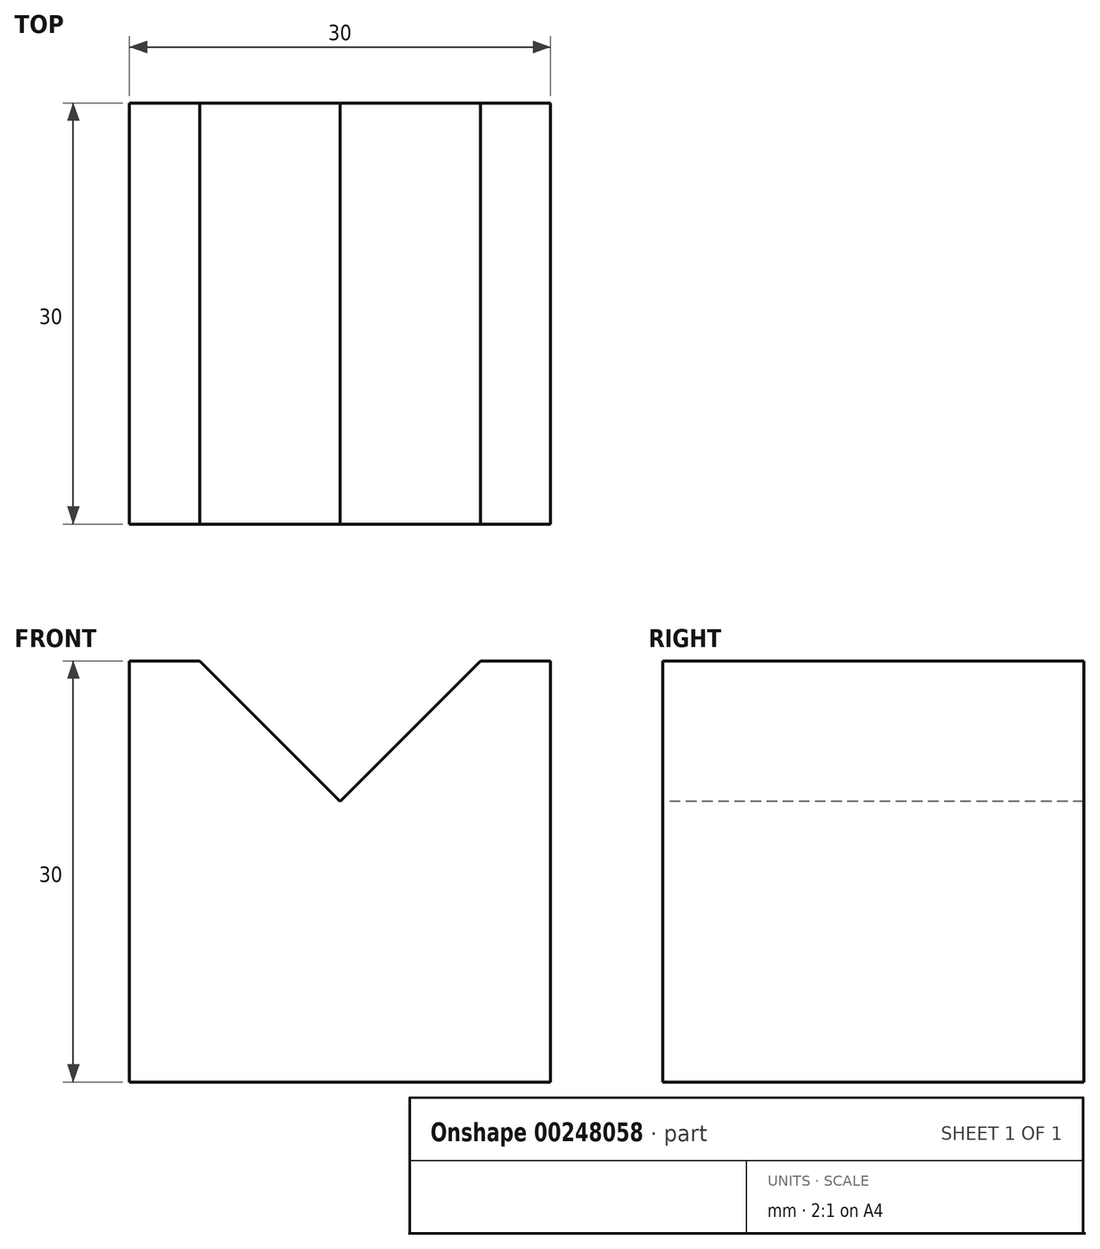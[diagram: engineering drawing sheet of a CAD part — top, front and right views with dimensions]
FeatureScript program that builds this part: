
annotation { "Feature Type Name" : "Feature", "Feature Type Description" : "" }
export const myFeature = defineFeature(function(context is Context, id is Id, definition is map)
    precondition{}
    {
        {
            var Q0;
            Q0=qCreatedBy(makeId("Top.planeOp"),FACE);
            var sketch = newSketch(context, id + "F0", { "sketchPlane" : qUnion([Q0])});
            skLineSegment(sketch, "E0.bottom", {"start": v(15, 15) * mm, "end": v(-15, 15) * mm});
            skLineSegment(sketch, "E0.top", {"start": v(15, -15) * mm, "end": v(-15, -15) * mm});
            skLineSegment(sketch, "E0.left", {"start": v(15, 15) * mm, "end": v(15, -15) * mm});
            skLineSegment(sketch, "E0.right", {"start": v(-15, 15) * mm, "end": v(-15, -15) * mm});
            skPoint(sketch, "E0.middle", {"position": v(0, 0) * mm});
            skSolve(sketch);
        }
        {
            var Q0;
            Q0 = qSketchRegion(id + "F0", true);
            extrude(context, id + "F1", {"entities" : qUnion([Q0]), "depth" : 30 * mm});
        }
        {
            var Q0;
            Q0=makeQuery(id+"F1.opExtrude","SWEPT_FACE",FACE,{"disambiguationData":[OSD([sQuery(id+"F0.wireOp",EDGE,"E0.top")])]});
            var sketch = newSketch(context, id + "F2", { "sketchPlane" : qUnion([Q0])});
            skLineSegment(sketch, "E1", {"start": v(-15, 30) * mm, "end": v(-10, 30) * mm, "construction": true});
            skLineSegment(sketch, "E2", {"start": v(-10, 30) * mm, "end": v(-10, 20) * mm, "construction": true});
            skLineSegment(sketch, "E3", {"start": v(-10, 20) * mm, "end": v(0, 20) * mm, "construction": true});
            skLineSegment(sketch, "E4", {"start": v(0, 20) * mm, "end": v(10, 20) * mm, "construction": true});
            skLineSegment(sketch, "E5", {"start": v(10, 20) * mm, "end": v(10, 30) * mm, "construction": true});
            skLineSegment(sketch, "E6", {"start": v(10, 30) * mm, "end": v(15, 30) * mm, "construction": true});
            skLineSegment(sketch, "E7", {"start": v(-10, 30) * mm, "end": v(0, 20) * mm});
            skLineSegment(sketch, "E8", {"start": v(10, 30) * mm, "end": v(0, 20) * mm});
            skSolve(sketch);
        }
        {
            var Q0;
            {var subQ0=sQuery(id+"F2.wireOp",EDGE,"E7");Q0=makeQuery(id+"F2.imprint","IMPRINT",FACE,{"disambiguationData":[TD([[makeQuery(id+"F2.imprint","IMPRINT",EDGE,{"derivedFrom":subQ0}),1.0]])]});}
            extrude(context, id + "F3", {"entities" : qUnion([Q0]), "operationType" : NewBodyOperationType.REMOVE, "endBound" : BoundingType.THROUGH_ALL, "oppositeDirection" : true, "depth" : 25 * mm});
        }
    });
